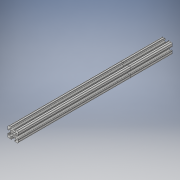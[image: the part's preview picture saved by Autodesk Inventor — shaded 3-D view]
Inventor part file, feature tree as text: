
AUTODESK INVENTOR PART (.ipt)
format: ipt  version: 2019 (Build 230136000, 136)  size: 323,072 bytes
history: native  units: in
note: dims shown in document units (in); Inventor stores cm internally (conversion verified against a paired STEP export)
features: other x3, extrude x1, sketch x1
ambient origin geometry x8: Origin, YZ Plane, XZ Plane, XY Plane, X Axis, Y Axis, Z Axis, Center Point
bodies: Solid1 (feature_tree), Solid2 (feature_tree)
feature tree (5):
  other  "16in 8020.iam"
  other  "1010.IPT:1"
  other  "1010.IPT:2"
  extrude  "Extrusion1"  Depth=0.3937in TaperAngle=0.0deg
  sketch  "Sketch1"  dims[d0=0.3937in d1=1.25in d2=0.0in]
